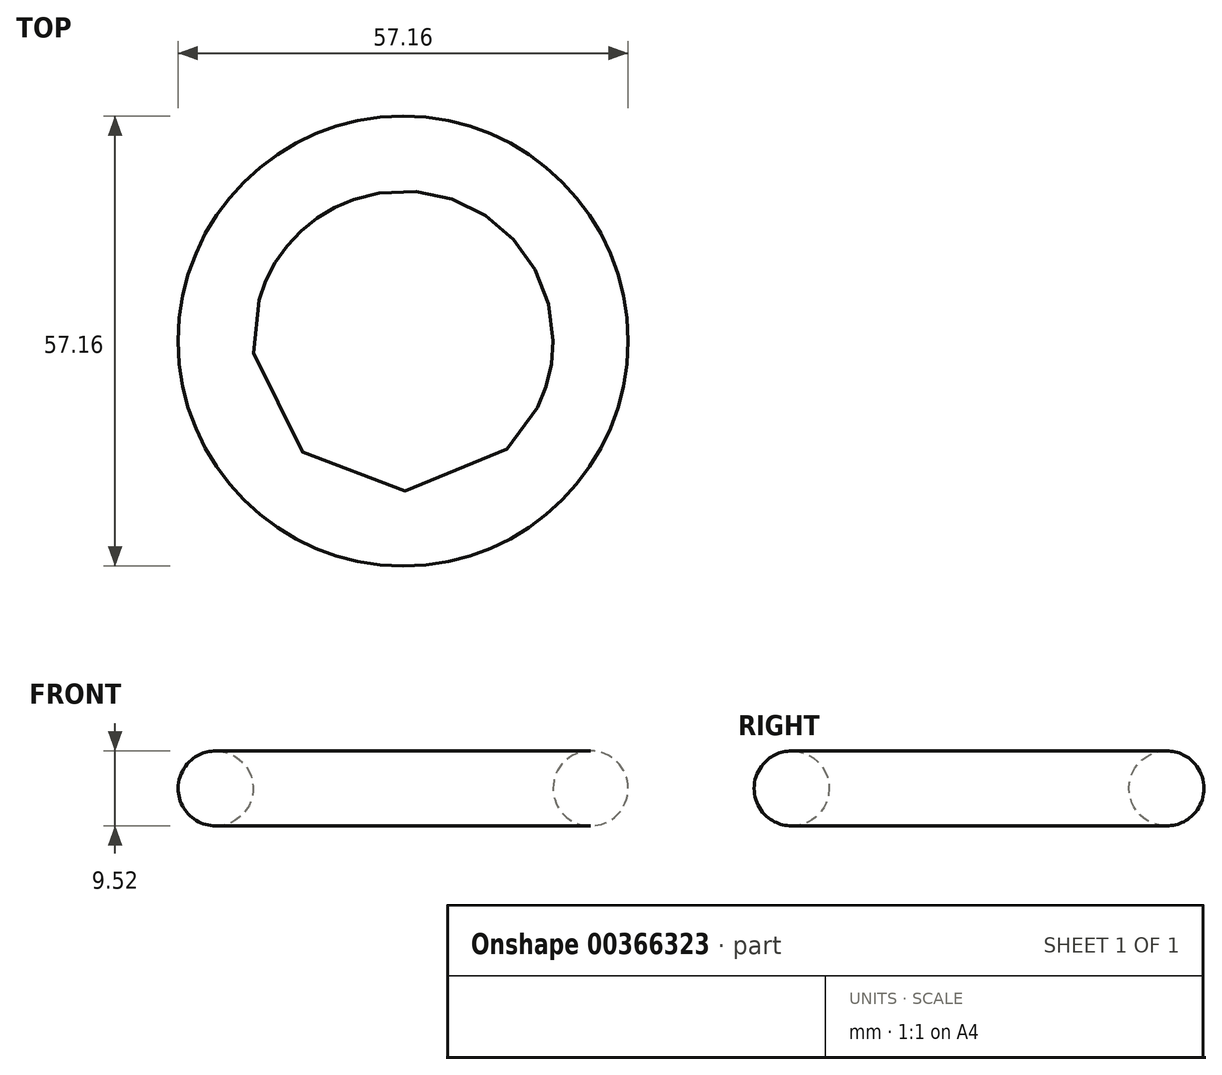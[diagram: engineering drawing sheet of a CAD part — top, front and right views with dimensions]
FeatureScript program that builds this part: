
annotation { "Feature Type Name" : "Feature", "Feature Type Description" : "" }
export const myFeature = defineFeature(function(context is Context, id is Id, definition is map)
    precondition{}
    {
        {
            var Q0;
            Q0=qCreatedBy(makeId("Front.planeOp"),FACE);
            var sketch = newSketch(context, id + "F0", { "sketchPlane" : qUnion([Q0])});
            skCircle(sketch, "E0", {"center": v(-23.81, 0) * mm, "radius": 4.76 * mm});
            skLineSegment(sketch, "E1", {"start": v(0, 12.67) * mm, "end": v(0, -12.47) * mm, "construction": true});
            skSolve(sketch);
        }
        {
            var Q0;
            Q0 = qSketchRegion(id + "F0", true);
            var Q1;
            Q1=sQuery(id+"F0.wireOp",EDGE,"E1");
            revolve(context, id + "F1", {"entities" : qUnion([Q0]), "axis" : qUnion([Q1]), "revolveType" : RevolveType.FULL});
        }
    });
